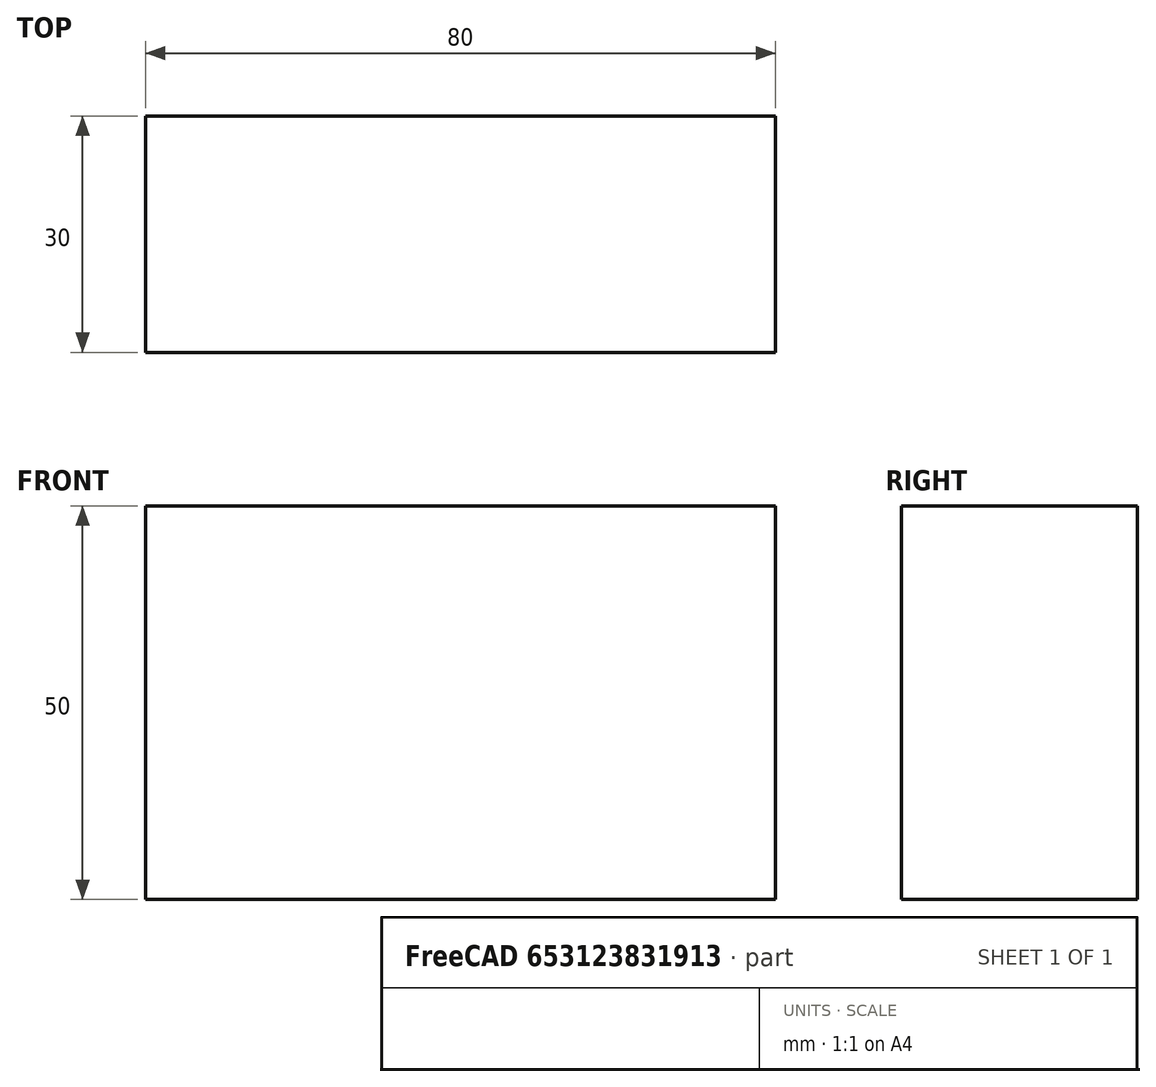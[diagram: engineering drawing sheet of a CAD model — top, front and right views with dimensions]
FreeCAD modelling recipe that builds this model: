
FCSTD DOCUMENT  (FreeCAD 0.15R4671 (Git))
Label: Flat Bar 80x30 EN10058 S235JR
License: All rights reserved
LicenseURL: http://en.wikipedia.org/wiki/All_rights_reserved
objects: Sketcher::SketchObject×1, Part::Extrusion×1
note: 2 computed .brp shape members not serialized (recipe doc carries the construction recipe); baked Part::Feature solids carry a one-line shape summary decoded from their .brp

FEATURE [Sketcher::SketchObject] Sketch
  sketch-geometry (4):
    g0: LineSegment StartX=-40 StartY=-15 StartZ=0 EndX=40 EndY=-15 EndZ=0
    g1: LineSegment StartX=40 StartY=-15 StartZ=0 EndX=40 EndY=15 EndZ=0
    g2: LineSegment StartX=40 StartY=15 StartZ=0 EndX=-40 EndY=15 EndZ=0
    g3: LineSegment StartX=-40 StartY=15 StartZ=0 EndX=-40 EndY=-15 EndZ=0
  constraints (12):
    c: Coincident(g0,g1)
    c: Coincident(g1,g2)
    c: Coincident(g2,g3)
    c: Coincident(g3,g0)
    c: Horizontal(g0)
    c: Horizontal(g2)
    c: Vertical(g1)
    c: Vertical(g3)
    c: Symmetric(g1,g2,g-2)
    c: Symmetric(g0,g1,g-1)
    c: DistanceY(g1) = 30
    c: DistanceX(g0) = 80
FEATURE [Part::Extrusion] Extrude  label="Flat Bar 80x30 EN10058 S235JR"
  Base = -> Sketch
  Dir = (0,0,50)
  Solid = true
